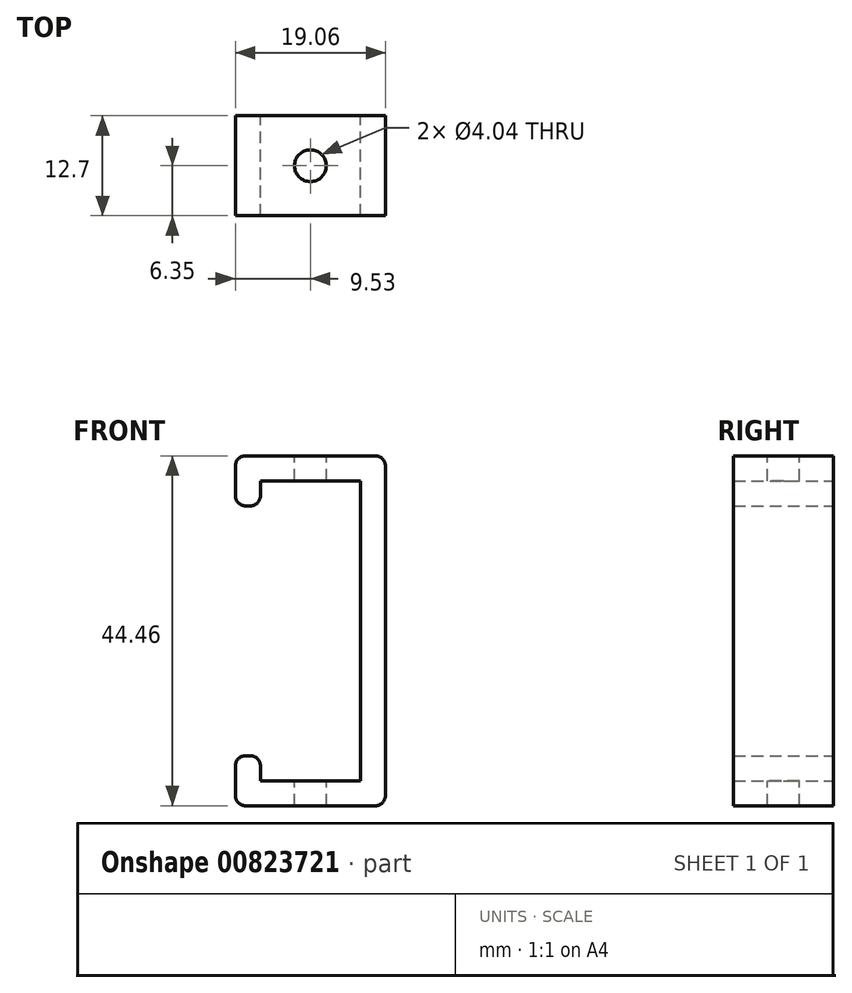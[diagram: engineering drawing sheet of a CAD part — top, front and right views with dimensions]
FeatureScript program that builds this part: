
annotation { "Feature Type Name" : "Feature", "Feature Type Description" : "" }
export const myFeature = defineFeature(function(context is Context, id is Id, definition is map)
    precondition{}
    {
        {
            var Q0;
            Q0=qCreatedBy(makeId("Front.planeOp"),FACE);
            var sketch = newSketch(context, id + "F0", { "sketchPlane" : qUnion([Q0])});
            skLineSegment(sketch, "E0.bottom", {"start": v(6.35, 19.05) * mm, "end": v(-6.35, 19.05) * mm});
            skLineSegment(sketch, "E0.top", {"start": v(6.35, -19.05) * mm, "end": v(-6.35, -19.05) * mm});
            skLineSegment(sketch, "E0.left", {"start": v(6.35, 19.05) * mm, "end": v(6.35, -19.05) * mm});
            skLineSegment(sketch, "E0.right", {"start": v(-6.35, 19.05) * mm, "end": v(-6.35, 15.88) * mm});
            skPoint(sketch, "E0.middle", {"position": v(0, 0) * mm});
            skLineSegment(sketch, "E1.bottom", {"start": v(9.53, 22.23) * mm, "end": v(-9.53, 22.23) * mm});
            skLineSegment(sketch, "E1.top", {"start": v(9.53, -22.23) * mm, "end": v(-9.53, -22.23) * mm});
            skLineSegment(sketch, "E1.left", {"start": v(9.53, 22.23) * mm, "end": v(9.53, -22.23) * mm});
            skLineSegment(sketch, "E1.right", {"start": v(-9.53, 22.23) * mm, "end": v(-9.53, 15.88) * mm});
            skLineSegment(sketch, "E2", {"start": v(-6.35, 15.88) * mm, "end": v(-9.52, 15.88) * mm});
            skLineSegment(sketch, "E3", {"start": v(-6.35, -15.88) * mm, "end": v(-9.53, -15.88) * mm});
            skLineSegment(sketch, "E4.trimOffspring", {"start": v(-6.35, -15.88) * mm, "end": v(-6.35, -19.05) * mm});
            skLineSegment(sketch, "E5.trimOffspring", {"start": v(-9.53, -15.88) * mm, "end": v(-9.53, -22.23) * mm});
            skSolve(sketch);
        }
        {
            var Q0;
            Q0=makeQuery(id+"F0.imprint","IMPRINT",FACE,{"disambiguationData":[TD([[makeQuery(id+"F0.imprint","IMPRINT",EDGE,{"derivedFrom":sQuery(id+"F0.wireOp",EDGE,"E0.bottom")}),-1.0]])]});
            extrude(context, id + "F1", {"entities" : qUnion([Q0]), "depth" : 6.35 * mm, "offsetDistance" : 25.4 * mm, "hasSecondDirection" : true, "secondDirectionOppositeDirection" : true, "secondDirectionDepth" : 6.35 * mm});
        }
        {
            var Q0;
            Q0=makeQuery(id+"F1.opExtrude","SWEPT_FACE",FACE,{"disambiguationData":[OSD([sQuery(id+"F0.wireOp",EDGE,"E1.bottom")])]});
            var sketch = newSketch(context, id + "F2", { "sketchPlane" : qUnion([Q0])});
            skPoint(sketch, "E6", {"position": v(0, 0) * mm});
            skSolve(sketch);
        }
        {
            var Q0;
            Q0=sQuery(id+"F2.wireOp",VERTEX,"E6");
            var Q1;
            Q1=makeQuery(id+"F1.opExtrude","SWEPT_BODY",BODY,{"disambiguationData":[OSD([sQuery(id+"F0.wireOp",EDGE,"E0.bottom"),sQuery(id+"F0.wireOp",EDGE,"E0.top"),sQuery(id+"F0.wireOp",EDGE,"E0.left"),sQuery(id+"F0.wireOp",EDGE,"E0.right"),sQuery(id+"F0.wireOp",EDGE,"E1.bottom"),sQuery(id+"F0.wireOp",EDGE,"E1.top"),sQuery(id+"F0.wireOp",EDGE,"E1.left"),sQuery(id+"F0.wireOp",EDGE,"E1.right"),sQuery(id+"F0.wireOp",EDGE,"E2"),sQuery(id+"F0.wireOp",EDGE,"E3"),sQuery(id+"F0.wireOp",EDGE,"E4.trimOffspring"),sQuery(id+"F0.wireOp",EDGE,"E5.trimOffspring")])]});
            hole(context, id + "F3", {"style" : HoleStyle.SIMPLE, "endStyle" : HoleEndStyle.THROUGH, "standardTappedOrClearance" : lookupTablePath({ "standard" : "ANSI", "engagement" : "75%", "pitch" : "32 tpi", "size" : "#10", "type" : "Tapped" }), "standardBlindInLast" : lookupTablePath({ "standard" : "ANSI", "engagement" : "75%", "pitch" : "32 tpi", "size" : "#10", "type" : "Tapped" }), "holeDiameter" : 4.04 * mm, "majorDiameter" : 4.83 * mm, "showTappedDepth" : true, "isTappedThrough" : true, "tappedDepth" : 12.7 * mm, "tapClearance" : 3, "locations" : qUnion([Q0]), "scope" : qUnion([Q1])});
        }
        {
            var Q0;
            Q0=makeQuery(id+"F1.opExtrude","SWEPT_EDGE",EDGE,{"disambiguationData":[OSD([sQuery(id+"F0.wireOp",EDGE,"E1.bottom"),sQuery(id+"F0.wireOp",EDGE,"E1.right")])]});
            var Q1;
            Q1=makeQuery(id+"F1.opExtrude","SWEPT_EDGE",EDGE,{"disambiguationData":[OSD([sQuery(id+"F0.wireOp",EDGE,"E1.right"),sQuery(id+"F0.wireOp",EDGE,"E2")])]});
            var Q2;
            Q2=makeQuery(id+"F1.opExtrude","SWEPT_EDGE",EDGE,{"disambiguationData":[OSD([sQuery(id+"F0.wireOp",EDGE,"E0.right"),sQuery(id+"F0.wireOp",EDGE,"E2")])]});
            var Q3;
            Q3=makeQuery(id+"F1.opExtrude","SWEPT_EDGE",EDGE,{"disambiguationData":[OSD([sQuery(id+"F0.wireOp",EDGE,"E1.bottom"),sQuery(id+"F0.wireOp",EDGE,"E1.left")])]});
            var Q4;
            Q4=makeQuery(id+"F1.opExtrude","SWEPT_EDGE",EDGE,{"disambiguationData":[OSD([sQuery(id+"F0.wireOp",EDGE,"E1.top"),sQuery(id+"F0.wireOp",EDGE,"E1.left")])]});
            var Q5;
            Q5=makeQuery(id+"F1.opExtrude","SWEPT_EDGE",EDGE,{"disambiguationData":[OSD([sQuery(id+"F0.wireOp",EDGE,"E1.top"),sQuery(id+"F0.wireOp",EDGE,"E5.trimOffspring")])]});
            var Q6;
            Q6=makeQuery(id+"F1.opExtrude","SWEPT_EDGE",EDGE,{"disambiguationData":[OSD([sQuery(id+"F0.wireOp",EDGE,"E3"),sQuery(id+"F0.wireOp",EDGE,"E5.trimOffspring")])]});
            var Q7;
            Q7=makeQuery(id+"F1.opExtrude","SWEPT_EDGE",EDGE,{"disambiguationData":[OSD([sQuery(id+"F0.wireOp",EDGE,"E3"),sQuery(id+"F0.wireOp",EDGE,"E4.trimOffspring")])]});
            fillet(context, id + "F4", {"entities" : qUnion([Q0, Q1, Q2, Q3, Q4, Q5, Q6, Q7]), "radius" : 1.27 * mm, "tangentPropagation" : true, "allowEdgeOverflow" : false});
        }
    });
